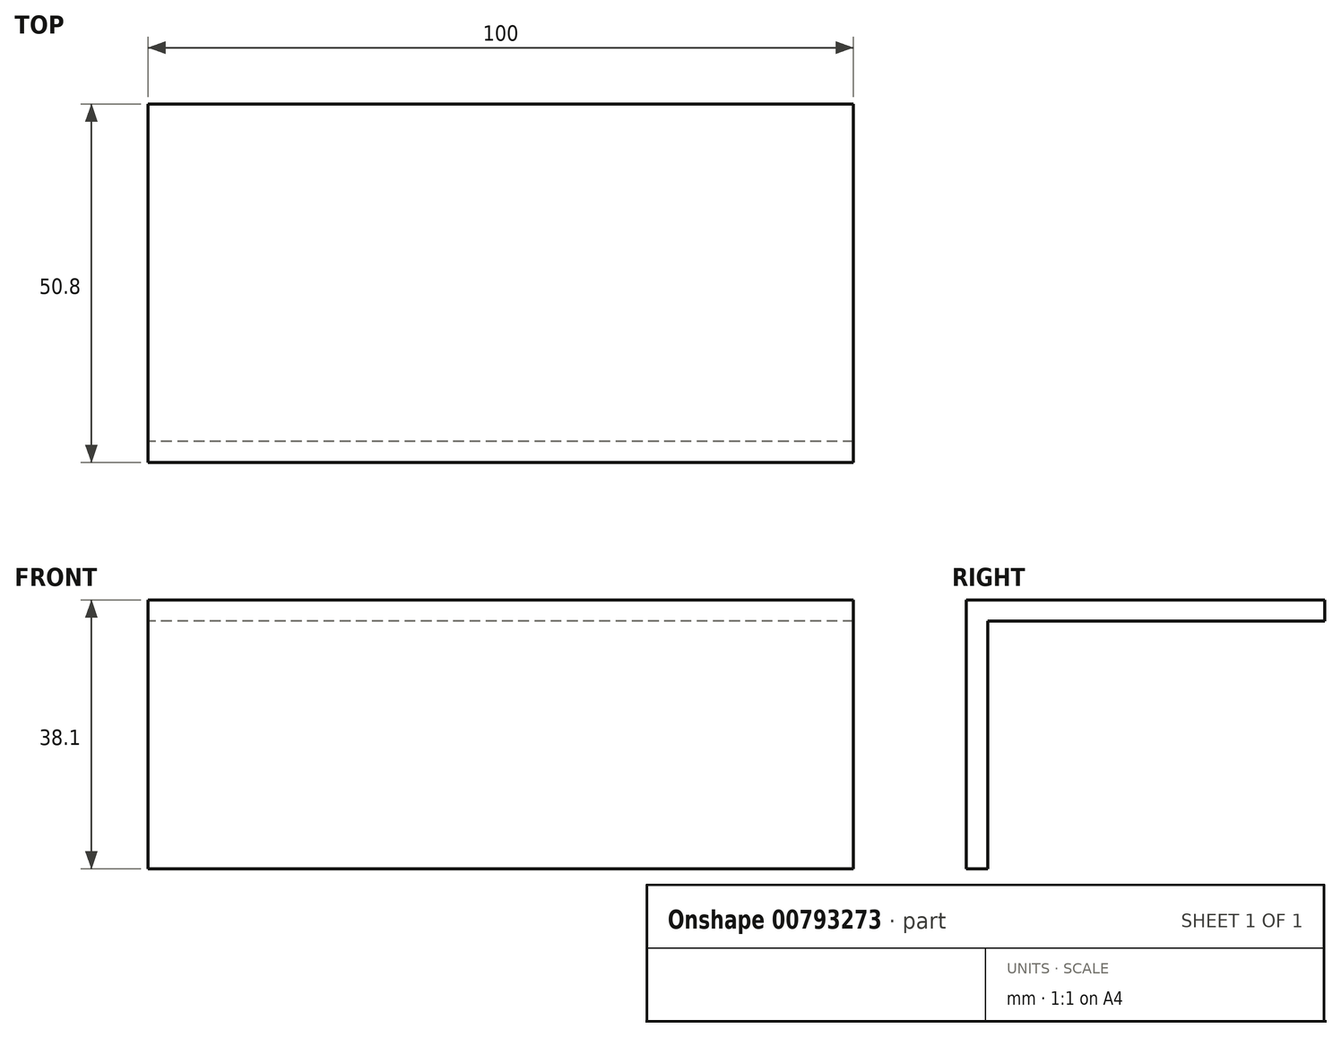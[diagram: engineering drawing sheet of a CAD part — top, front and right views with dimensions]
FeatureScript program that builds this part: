
annotation { "Feature Type Name" : "Feature", "Feature Type Description" : "" }
export const myFeature = defineFeature(function(context is Context, id is Id, definition is map)
    precondition{}
    {
        {
            var Q0;
            Q0=qCreatedBy(makeId("Right.planeOp"),FACE);
            var sketch = newSketch(context, id + "F0", { "sketchPlane" : qUnion([Q0])});
            skLineSegment(sketch, "E0", {"start": v(50.8, 0) * mm, "end": v(0, 0) * mm});
            skLineSegment(sketch, "E1", {"start": v(0, 0) * mm, "end": v(0, -38.1) * mm});
            skLineSegment(sketch, "E2.0", {"start": v(3, -3) * mm, "end": v(3, -38.1) * mm});
            skLineSegment(sketch, "E2.1", {"start": v(50.8, -3) * mm, "end": v(3, -3) * mm});
            skLineSegment(sketch, "E3", {"start": v(50.8, -3) * mm, "end": v(50.8, 0) * mm});
            skLineSegment(sketch, "E4", {"start": v(3, -38.1) * mm, "end": v(0, -38.1) * mm});
            skSolve(sketch);
        }
        {
            var Q0;
            Q0=makeQuery(id+"F0.imprint","IMPRINT",FACE,{"disambiguationData":[TD([[makeQuery(id+"F0.imprint","IMPRINT",EDGE,{"derivedFrom":sQuery(id+"F0.wireOp",EDGE,"E0")}),1.0]])]});
            extrude(context, id + "F1", {"entities" : qUnion([Q0]), "depth" : 100 * mm, "offsetDistance" : 25 * mm});
        }
    });
